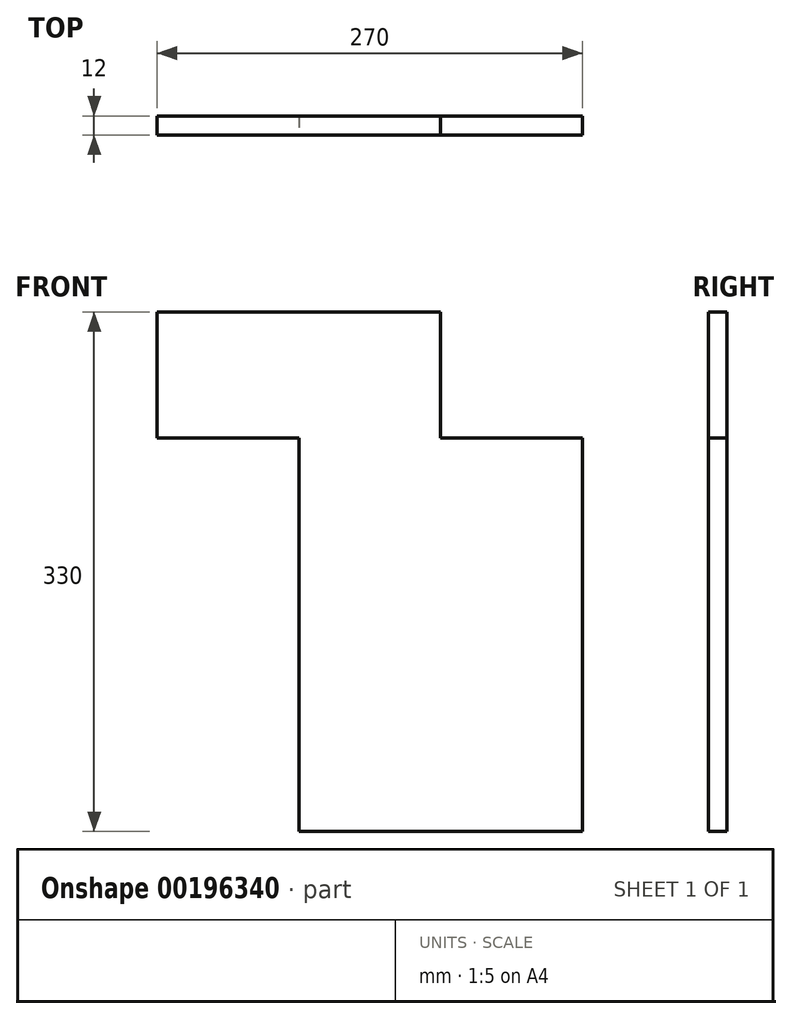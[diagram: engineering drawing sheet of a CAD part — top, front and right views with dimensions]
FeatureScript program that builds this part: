
annotation { "Feature Type Name" : "Feature", "Feature Type Description" : "" }
export const myFeature = defineFeature(function(context is Context, id is Id, definition is map)
    precondition{}
    {
        {
            var Q0;
            Q0=qCreatedBy(makeId("Front.planeOp"),FACE);
            var sketch = newSketch(context, id + "F0", { "sketchPlane" : qUnion([Q0])});
            skLineSegment(sketch, "E0.bottom", {"start": v(-57.36, 55.7) * mm, "end": v(122.64, 55.7) * mm});
            skLineSegment(sketch, "E0.top", {"start": v(-57.36, -194.3) * mm, "end": v(122.64, -194.3) * mm});
            skLineSegment(sketch, "E0.left", {"start": v(-57.36, 55.7) * mm, "end": v(-57.36, -194.3) * mm});
            skLineSegment(sketch, "E0.right", {"start": v(122.64, 55.7) * mm, "end": v(122.64, -194.3) * mm});
            skSolve(sketch);
        }
        {
            var Q0;
            Q0=makeQuery(id+"F0.imprint","IMPRINT",FACE,{"disambiguationData":[TD([[makeQuery(id+"F0.imprint","IMPRINT",EDGE,{"derivedFrom":sQuery(id+"F0.wireOp",EDGE,"E0.bottom")}),-1.0]])]});
            extrude(context, id + "F1", {"entities" : qUnion([Q0]), "oppositeDirection" : true, "depth" : 12 * mm});
        }
        {
            var Q0;
            Q0=makeQuery(id+"F1.opExtrude","CAP_FACE",FACE,{"disambiguationData":[OSD([sQuery(id+"F0.wireOp",EDGE,"E0.bottom"),sQuery(id+"F0.wireOp",EDGE,"E0.top"),sQuery(id+"F0.wireOp",EDGE,"E0.left"),sQuery(id+"F0.wireOp",EDGE,"E0.right")])],"isStart":true});
            var sketch = newSketch(context, id + "F2", { "sketchPlane" : qUnion([Q0])});
            skLineSegment(sketch, "E1", {"start": v(32.64, 55.7) * mm, "end": v(32.64, 135.7) * mm});
            skPoint(sketch, "E1.endSnap0", {"position": v(32.64, 55.7) * mm});
            skLineSegment(sketch, "E2", {"start": v(32.64, 135.7) * mm, "end": v(-147.36, 135.7) * mm});
            skLineSegment(sketch, "E3", {"start": v(-147.36, 135.7) * mm, "end": v(-147.36, 55.7) * mm});
            skLineSegment(sketch, "E4", {"start": v(-147.36, 55.7) * mm, "end": v(32.64, 55.7) * mm});
            skSolve(sketch);
        }
        {
            var Q0;
            Q0 = qSketchRegion(id + "F2", true);
            extrude(context, id + "F3", {"entities" : qUnion([Q0]), "operationType" : NewBodyOperationType.ADD, "oppositeDirection" : true, "depth" : 12 * mm});
        }
    });
